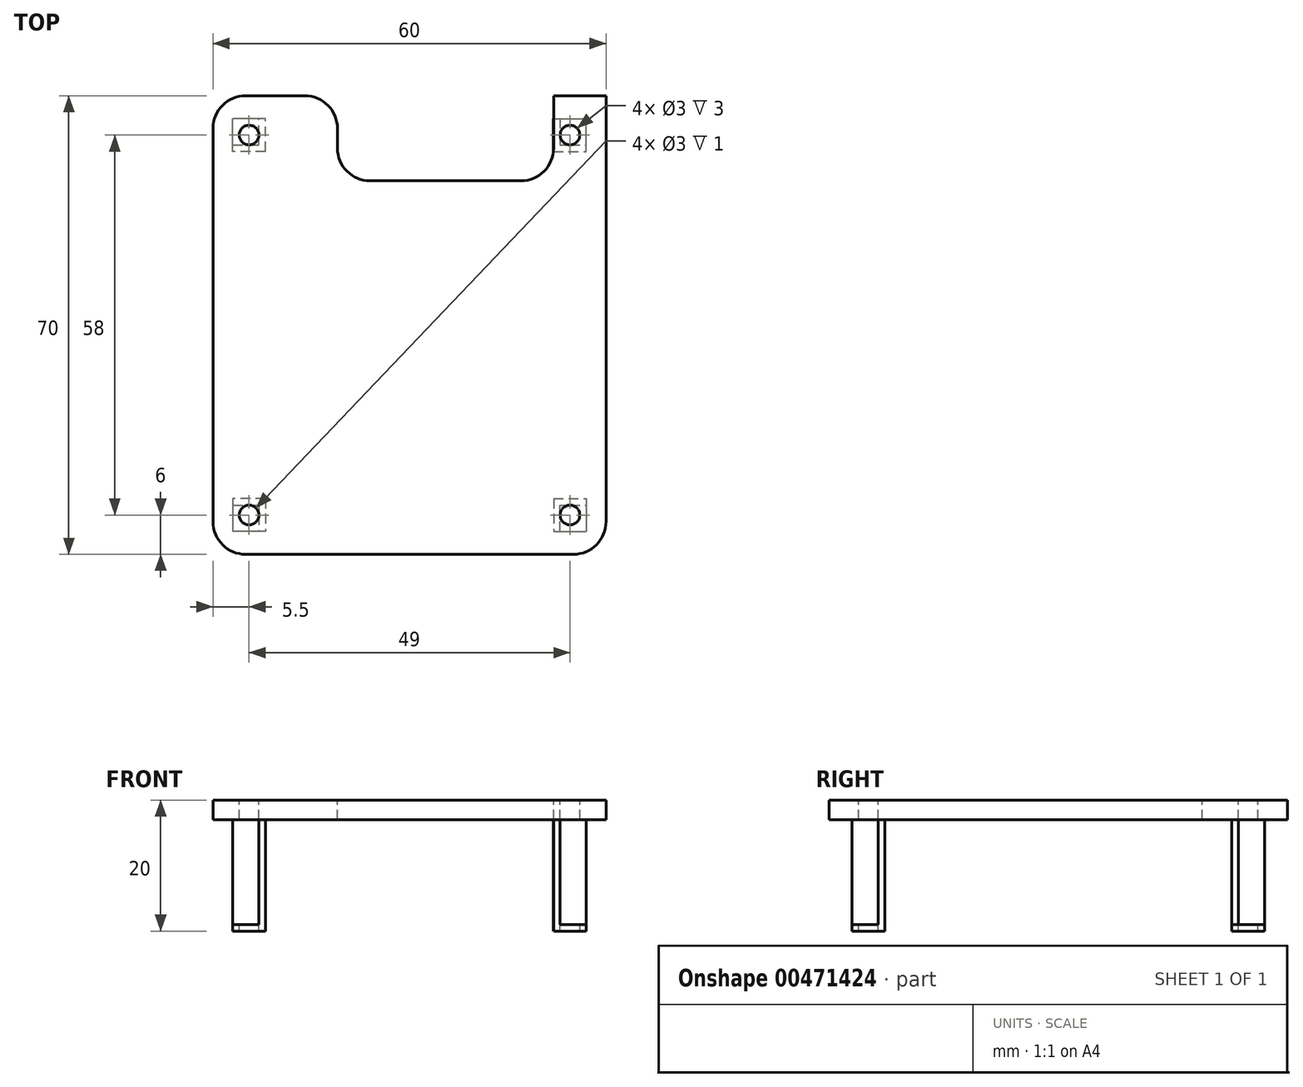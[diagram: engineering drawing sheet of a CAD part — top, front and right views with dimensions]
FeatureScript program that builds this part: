
annotation { "Feature Type Name" : "Feature", "Feature Type Description" : "" }
export const myFeature = defineFeature(function(context is Context, id is Id, definition is map)
    precondition{}
    {
        {
            var Q0;
            Q0=qCreatedBy(makeId("Top.planeOp"),FACE);
            var sketch = newSketch(context, id + "F0", { "sketchPlane" : qUnion([Q0])});
            skLineSegment(sketch, "E0.bottom", {"start": v(30, 35) * mm, "end": v(22, 35) * mm});
            skLineSegment(sketch, "E0.top", {"start": v(30, -35) * mm, "end": v(-30, -35) * mm});
            skLineSegment(sketch, "E0.left", {"start": v(30, 35) * mm, "end": v(30, -35) * mm});
            skLineSegment(sketch, "E0.right", {"start": v(-30, 35) * mm, "end": v(-30, -35) * mm});
            skPoint(sketch, "E0.middle", {"position": v(0, 0) * mm});
            skCircle(sketch, "E1", {"center": v(-24.5, 29) * mm, "radius": 1.5 * mm});
            skCircle(sketch, "E2.MirrorC", {"center": v(24.5, 29) * mm, "radius": 1.5 * mm});
            skCircle(sketch, "E3.MirrorC", {"center": v(-24.5, -29) * mm, "radius": 1.5 * mm});
            skCircle(sketch, "E4.MirrorC", {"center": v(24.5, -29) * mm, "radius": 1.5 * mm});
            skLineSegment(sketch, "E5", {"start": v(22, 35) * mm, "end": v(22, 22) * mm});
            skLineSegment(sketch, "E6", {"start": v(22, 22) * mm, "end": v(-11, 22) * mm});
            skLineSegment(sketch, "E7", {"start": v(-11, 22) * mm, "end": v(-11, 35) * mm});
            skLineSegment(sketch, "E8.trimOffspring", {"start": v(-11, 35) * mm, "end": v(-30, 35) * mm});
            skSolve(sketch);
        }
        {
            var Q0;
            Q0 = qSketchRegion(id + "F0", true);
            extrude(context, id + "F1", {"entities" : qUnion([Q0]), "oppositeDirection" : true, "depth" : 3 * mm});
        }
        {
            var Q0;
            Q0=makeQuery(id+"F1.opExtrude","CAP_FACE",FACE,{"disambiguationData":[OSD([sQuery(id+"F0.wireOp",EDGE,"E0.bottom"),sQuery(id+"F0.wireOp",EDGE,"E0.top"),sQuery(id+"F0.wireOp",EDGE,"E0.left"),sQuery(id+"F0.wireOp",EDGE,"E0.right"),sQuery(id+"F0.wireOp",EDGE,"E1"),sQuery(id+"F0.wireOp",EDGE,"E2.MirrorC"),sQuery(id+"F0.wireOp",EDGE,"E3.MirrorC"),sQuery(id+"F0.wireOp",EDGE,"E4.MirrorC"),sQuery(id+"F0.wireOp",EDGE,"E5"),sQuery(id+"F0.wireOp",EDGE,"E6"),sQuery(id+"F0.wireOp",EDGE,"E7"),sQuery(id+"F0.wireOp",EDGE,"E8.trimOffspring")])],"isStart":false});
            var sketch = newSketch(context, id + "F2", { "sketchPlane" : qUnion([Q0])});
            skLineSegment(sketch, "E9.bottom", {"start": v(22, -26.5) * mm, "end": v(27, -26.5) * mm});
            skLineSegment(sketch, "E9.left", {"start": v(22, -26.5) * mm, "end": v(22, -31.5) * mm});
            skPoint(sketch, "E9.middle", {"position": v(24.5, -29) * mm});
            skLineSegment(sketch, "E10.MirrorCS", {"start": v(22, 26.5) * mm, "end": v(27, 26.5) * mm});
            skLineSegment(sketch, "E11.MirrorCS", {"start": v(22, 26.5) * mm, "end": v(22, 31.5) * mm});
            skLineSegment(sketch, "E12.MirrorCS", {"start": v(-22, -26.5) * mm, "end": v(-27, -26.5) * mm});
            skLineSegment(sketch, "E13.MirrorCS", {"start": v(-22, -26.5) * mm, "end": v(-22, -31.5) * mm});
            skLineSegment(sketch, "E14.MirrorCS", {"start": v(-22, 26.5) * mm, "end": v(-27, 26.5) * mm});
            skLineSegment(sketch, "E15.MirrorCS", {"start": v(-22, 26.5) * mm, "end": v(-22, 31.5) * mm});
            skCircle(sketch, "E16.0", {"center": v(-24.5, -29) * mm, "radius": 1.5 * mm});
            skCircle(sketch, "E17.0", {"center": v(24.5, -29) * mm, "radius": 1.5 * mm});
            skCircle(sketch, "E18.0", {"center": v(24.5, 29) * mm, "radius": 1.5 * mm});
            skCircle(sketch, "E18.1", {"center": v(-24.5, 29) * mm, "radius": 1.5 * mm});
            skLineSegment(sketch, "E19", {"start": v(27, -26.5) * mm, "end": v(27, -27.5) * mm});
            skLineSegment(sketch, "E20", {"start": v(22, -31.5) * mm, "end": v(23, -31.5) * mm});
            skLineSegment(sketch, "E21", {"start": v(23, -31.5) * mm, "end": v(23, -27.5) * mm});
            skLineSegment(sketch, "E22", {"start": v(23, -27.5) * mm, "end": v(27, -27.5) * mm});
            skLineSegment(sketch, "E23", {"start": v(-22, -31.5) * mm, "end": v(-23, -31.5) * mm});
            skLineSegment(sketch, "E24", {"start": v(-27, -26.5) * mm, "end": v(-27, -27.5) * mm});
            skLineSegment(sketch, "E25", {"start": v(-27, -27.5) * mm, "end": v(-23, -27.5) * mm});
            skLineSegment(sketch, "E26", {"start": v(-23, -27.5) * mm, "end": v(-23, -31.5) * mm});
            skLineSegment(sketch, "E27", {"start": v(27, 26.5) * mm, "end": v(27, 27.5) * mm});
            skLineSegment(sketch, "E28", {"start": v(22, 31.5) * mm, "end": v(23, 31.5) * mm});
            skLineSegment(sketch, "E29", {"start": v(23, 31.5) * mm, "end": v(23, 27.5) * mm});
            skLineSegment(sketch, "E30", {"start": v(23, 27.5) * mm, "end": v(27, 27.5) * mm});
            skLineSegment(sketch, "E31", {"start": v(-27, 26.5) * mm, "end": v(-27, 27.5) * mm});
            skLineSegment(sketch, "E32", {"start": v(-22, 31.5) * mm, "end": v(-23, 31.5) * mm});
            skLineSegment(sketch, "E33", {"start": v(-27, 27.5) * mm, "end": v(-23, 27.5) * mm});
            skLineSegment(sketch, "E34", {"start": v(-23, 27.5) * mm, "end": v(-23, 31.5) * mm});
            skSolve(sketch);
        }
        {
            var Q0;
            Q0=makeQuery(id+"F2.imprint","IMPRINT",FACE,{"disambiguationData":[TD([[makeQuery(id+"F2.imprint","IMPRINT",EDGE,{"derivedFrom":sQuery(id+"F2.wireOp",EDGE,"E9.bottom")}),-1.0]])]});
            var Q1;
            Q1=makeQuery(id+"F2.imprint","IMPRINT",FACE,{"disambiguationData":[TD([[makeQuery(id+"F2.imprint","IMPRINT",EDGE,{"derivedFrom":sQuery(id+"F2.wireOp",EDGE,"E12.MirrorCS")}),1.0]])]});
            var Q2;
            Q2=makeQuery(id+"F2.imprint","IMPRINT",FACE,{"disambiguationData":[TD([[makeQuery(id+"F2.imprint","IMPRINT",EDGE,{"derivedFrom":sQuery(id+"F2.wireOp",EDGE,"E14.MirrorCS")}),-1.0]])]});
            var Q3;
            Q3=makeQuery(id+"F2.imprint","IMPRINT",FACE,{"disambiguationData":[TD([[makeQuery(id+"F2.imprint","IMPRINT",EDGE,{"derivedFrom":sQuery(id+"F2.wireOp",EDGE,"E10.MirrorCS")}),1.0]])]});
            extrude(context, id + "F3", {"entities" : qUnion([Q0, Q1, Q2, Q3]), "operationType" : NewBodyOperationType.ADD, "depth" : 16 * mm, "offsetDistance" : 25 * mm});
        }
        {
            var Q0;
            Q0=makeQuery(id+"F1.opExtrude","SWEPT_EDGE",EDGE,{"disambiguationData":[OSD([sQuery(id+"F0.wireOp",EDGE,"E0.right"),sQuery(id+"F0.wireOp",EDGE,"E8.trimOffspring")])]});
            var Q1;
            Q1=makeQuery(id+"F1.opExtrude","SWEPT_EDGE",EDGE,{"disambiguationData":[OSD([sQuery(id+"F0.wireOp",EDGE,"E0.top"),sQuery(id+"F0.wireOp",EDGE,"E0.right")])]});
            var Q2;
            Q2=makeQuery(id+"F1.opExtrude","SWEPT_EDGE",EDGE,{"disambiguationData":[OSD([sQuery(id+"F0.wireOp",EDGE,"E7"),sQuery(id+"F0.wireOp",EDGE,"E8.trimOffspring")])]});
            var Q3;
            Q3=makeQuery(id+"F1.opExtrude","SWEPT_EDGE",EDGE,{"disambiguationData":[OSD([sQuery(id+"F0.wireOp",EDGE,"E6"),sQuery(id+"F0.wireOp",EDGE,"E7")])]});
            var Q4;
            Q4=makeQuery(id+"F1.opExtrude","SWEPT_EDGE",EDGE,{"disambiguationData":[OSD([sQuery(id+"F0.wireOp",EDGE,"E5"),sQuery(id+"F0.wireOp",EDGE,"E6")])]});
            var Q5;
            Q5=makeQuery(id+"F1.opExtrude","SWEPT_EDGE",EDGE,{"disambiguationData":[OSD([sQuery(id+"F0.wireOp",EDGE,"E0.top"),sQuery(id+"F0.wireOp",EDGE,"E0.left")])]});
            fillet(context, id + "F4", {"entities" : qUnion([Q0, Q1, Q2, Q3, Q4, Q5]), "radius" : 5 * mm, "tangentPropagation" : true, "allowEdgeOverflow" : false});
        }
        {
            var Q0;
            Q0=makeQuery(id+"F3.opExtrude","CAP_FACE",FACE,{"disambiguationData":[OSD([sQuery(id+"F2.wireOp",EDGE,"E14.MirrorCS"),sQuery(id+"F2.wireOp",EDGE,"E15.MirrorCS"),sQuery(id+"F2.wireOp",EDGE,"E31"),sQuery(id+"F2.wireOp",EDGE,"E32"),sQuery(id+"F2.wireOp",EDGE,"E33"),sQuery(id+"F2.wireOp",EDGE,"E34")])],"isStart":false});
            var sketch = newSketch(context, id + "F5", { "sketchPlane" : qUnion([Q0])});
            skPoint(sketch, "E35.oppositeSnap0", {"position": v(-22.5, 31.5) * mm});
            skLineSegment(sketch, "E35.bottom", {"start": v(-22, 26.5) * mm, "end": v(-27, 26.5) * mm});
            skLineSegment(sketch, "E35.top", {"start": v(-22, 31.5) * mm, "end": v(-27, 31.5) * mm});
            skLineSegment(sketch, "E35.left", {"start": v(-22, 26.5) * mm, "end": v(-22, 31.5) * mm});
            skLineSegment(sketch, "E35.right", {"start": v(-27, 26.5) * mm, "end": v(-27, 31.5) * mm});
            skPoint(sketch, "E36.0", {"position": v(22, 26.5) * mm});
            skLineSegment(sketch, "E37.bottom", {"start": v(22, 26.5) * mm, "end": v(27, 26.5) * mm});
            skLineSegment(sketch, "E37.top", {"start": v(22, 31.5) * mm, "end": v(27, 31.5) * mm});
            skLineSegment(sketch, "E37.left", {"start": v(22, 26.5) * mm, "end": v(22, 31.5) * mm});
            skLineSegment(sketch, "E37.right", {"start": v(27, 26.5) * mm, "end": v(27, 31.5) * mm});
            skPoint(sketch, "E38.0", {"position": v(21.97, -26.5) * mm});
            skPoint(sketch, "E38.1", {"position": v(-22, -26.5) * mm});
            skLineSegment(sketch, "E39.bottom", {"start": v(21.97, -26.5) * mm, "end": v(26.97, -26.5) * mm});
            skLineSegment(sketch, "E39.top", {"start": v(21.97, -31.5) * mm, "end": v(26.97, -31.5) * mm});
            skLineSegment(sketch, "E39.left", {"start": v(21.97, -26.5) * mm, "end": v(21.97, -31.5) * mm});
            skLineSegment(sketch, "E39.right", {"start": v(26.97, -26.5) * mm, "end": v(26.97, -31.5) * mm});
            skLineSegment(sketch, "E40.bottom", {"start": v(-22, -26.5) * mm, "end": v(-27, -26.5) * mm});
            skLineSegment(sketch, "E40.top", {"start": v(-22, -31.5) * mm, "end": v(-27, -31.5) * mm});
            skLineSegment(sketch, "E40.left", {"start": v(-22, -26.5) * mm, "end": v(-22, -31.5) * mm});
            skLineSegment(sketch, "E40.right", {"start": v(-27, -26.5) * mm, "end": v(-27, -31.5) * mm});
            skArc(sketch, "E41.0", {"start": v(23, 29) * mm, "mid": v(25.56, 30.06) * mm, "end": v(24.5, 27.5) * mm});
            skArc(sketch, "E42.0", {"start": v(24.5, 27.5) * mm, "mid": v(23.44, 27.94) * mm, "end": v(23, 29) * mm});
            skArc(sketch, "E43.0", {"start": v(-23, 29) * mm, "mid": v(-25.56, 30.06) * mm, "end": v(-24.5, 27.5) * mm});
            skArc(sketch, "E43.1", {"start": v(-24.5, 27.5) * mm, "mid": v(-23.44, 27.94) * mm, "end": v(-23, 29) * mm});
            skArc(sketch, "E44.0", {"start": v(-23, -29) * mm, "mid": v(-25.56, -30.06) * mm, "end": v(-24.5, -27.5) * mm});
            skArc(sketch, "E44.1", {"start": v(-24.5, -27.5) * mm, "mid": v(-23.44, -27.94) * mm, "end": v(-23, -29) * mm});
            skArc(sketch, "E45.0", {"start": v(23, -29) * mm, "mid": v(25.56, -30.06) * mm, "end": v(24.5, -27.5) * mm});
            skArc(sketch, "E45.1", {"start": v(24.5, -27.5) * mm, "mid": v(23.44, -27.94) * mm, "end": v(23, -29) * mm});
            skSolve(sketch);
        }
        {
            var Q0;
            Q0 = qSketchRegion(id + "F5", true);
            extrude(context, id + "F6", {"entities" : qUnion([Q0]), "operationType" : NewBodyOperationType.ADD, "depth" : 1 * mm, "offsetDistance" : 25 * mm});
        }
    });
